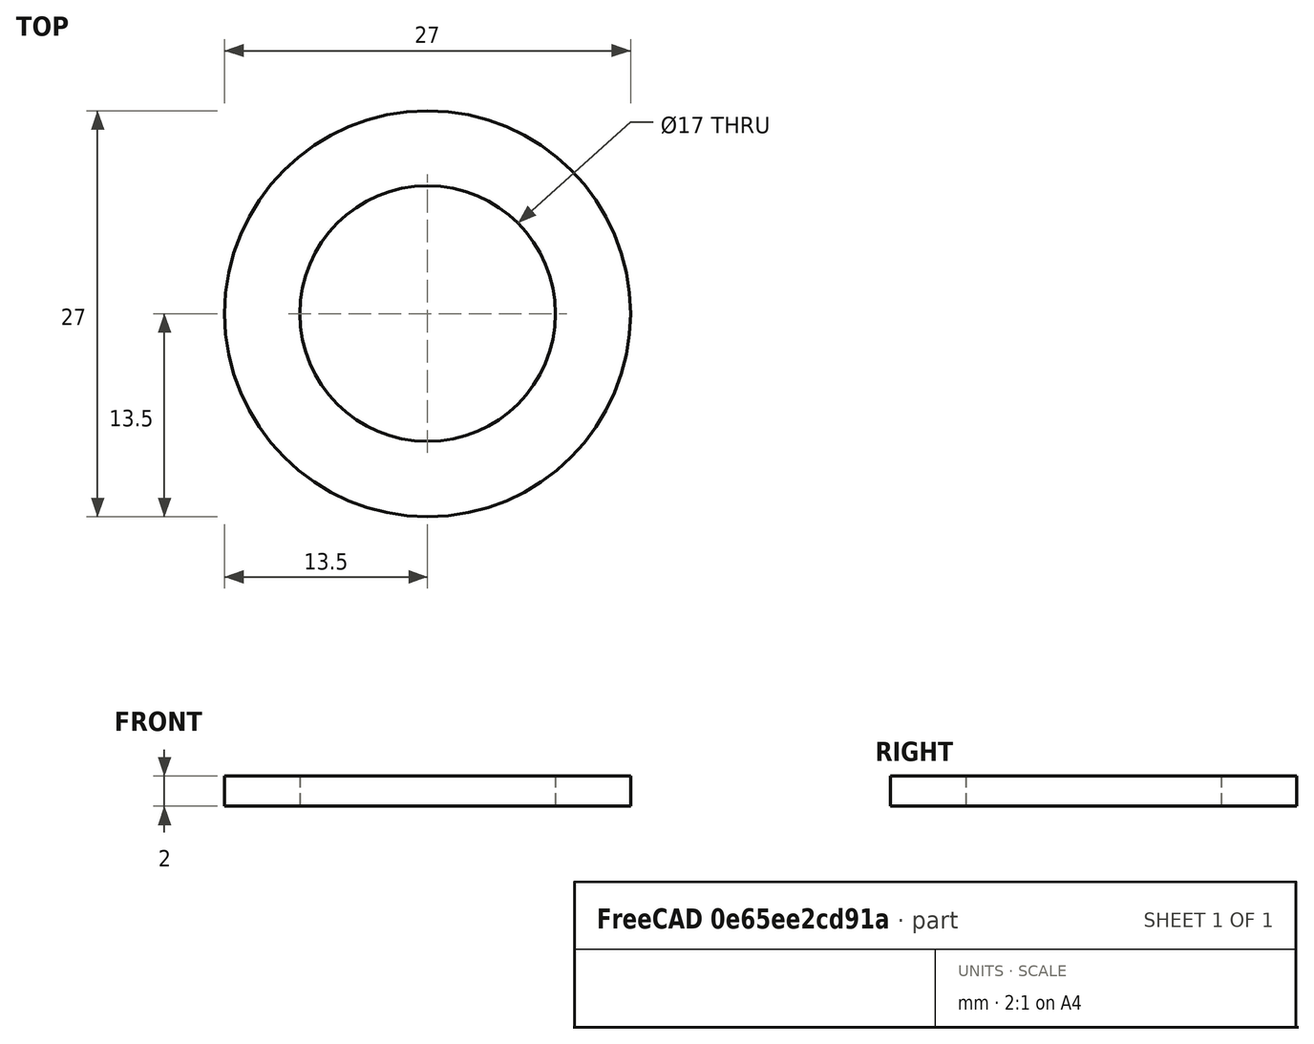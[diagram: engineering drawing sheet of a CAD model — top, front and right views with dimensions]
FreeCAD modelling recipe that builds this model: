
FCSTD DOCUMENT  (FreeCAD 0.14R3700 (Git))
Label: Scheibe DIN 433 - A 17
License: CC-BY 3.0
LicenseURL: http://creativecommons.org/licenses/by/3.0/
objects: Sketcher::SketchObject×1, PartDesign::Revolution×1, Part::Feature×1
note: 4 computed .brp shape members not serialized (recipe doc carries the construction recipe); baked Part::Feature solids carry a one-line shape summary decoded from their .brp

FEATURE [Sketcher::SketchObject] Sketch
  Placement = pos=(0,0,0) rot=(0.57735,0.57735,0.57735;2.0944rad)
  sketch-geometry (4):
    g0: LineSegment StartX=8.5 StartY=0 StartZ=0 EndX=13.5 EndY=0 EndZ=0
    g1: LineSegment StartX=13.5 StartY=0 StartZ=0 EndX=13.5 EndY=2 EndZ=0
    g2: LineSegment StartX=13.5 StartY=2 StartZ=0 EndX=8.5 EndY=2 EndZ=0
    g3: LineSegment StartX=8.5 StartY=2 StartZ=0 EndX=8.5 EndY=0 EndZ=0
  constraints (12):
    c: Coincident(g0,g1)
    c: Coincident(g1,g2)
    c: Coincident(g2,g3)
    c: Coincident(g3,g0)
    c: Horizontal(g0)
    c: Horizontal(g2)
    c: Vertical(g1)
    c: Vertical(g3)
    c: PointOnObject(g0,g-1)
    c: DistanceY(g1) = 2
    c: DistanceX(g-1,g2) = 8.5
    c: DistanceX(g-1,g1) = 13.5
FEATURE [PartDesign::Revolution] Revolution  label="Scheibe DIN 433 - A 17 #"
  Angle = 360
  Axis = (0,0,1)
  Base = (0,0,0)
  Placement = pos=(0,0,0) rot=(0.57735,0.57735,0.57735;2.0944rad)
  ReferenceAxis = -> Sketch [V_Axis]
  Reversed = true
  Sketch = -> Sketch
FEATURE [Part::Feature] Revolution001  label="Scheibe DIN 433 - A 17 #001"
  Placement = pos=(0,0,0) rot=(0.57735,0.57735,0.57735;2.0944rad)
  shape: bbox 27 x 27 x 2 mm, 4 faces (baked)
